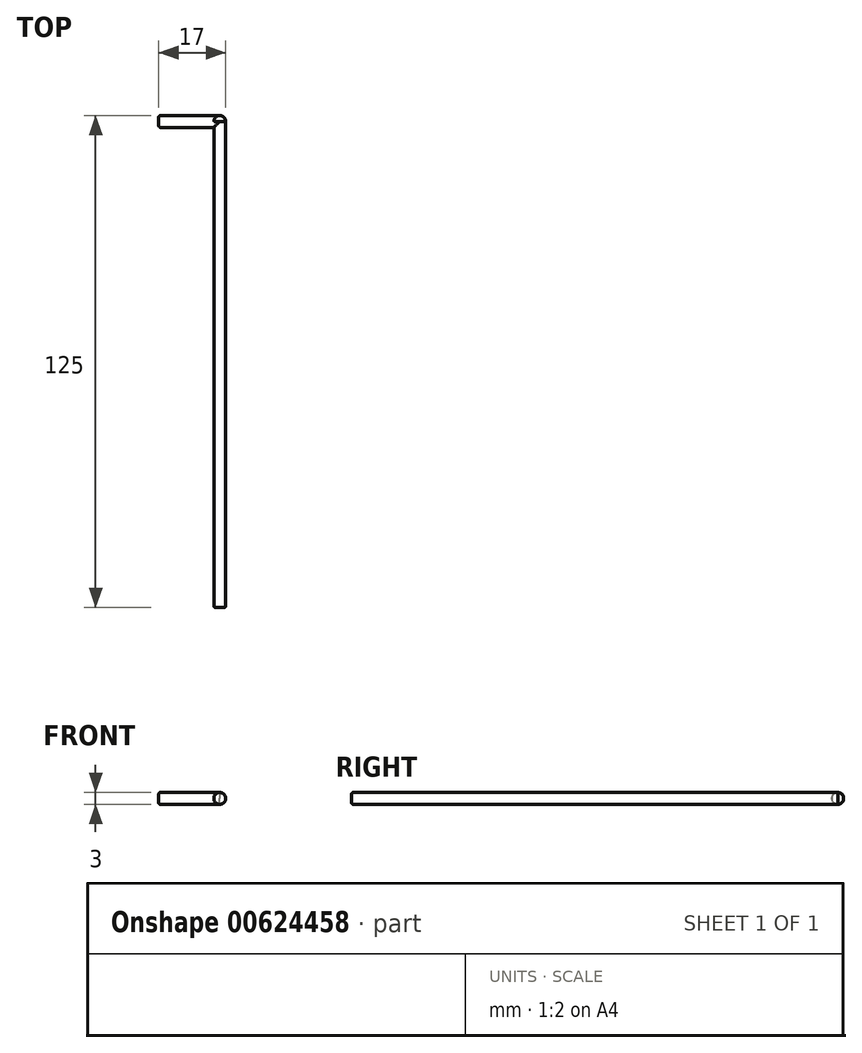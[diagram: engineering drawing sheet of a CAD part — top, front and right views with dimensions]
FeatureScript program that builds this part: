
annotation { "Feature Type Name" : "Feature", "Feature Type Description" : "" }
export const myFeature = defineFeature(function(context is Context, id is Id, definition is map)
    precondition{}
    {
        {
            var Q0;
            Q0=qCreatedBy(makeId("Front.planeOp"),FACE);
            var sketch = newSketch(context, id + "F0", { "sketchPlane" : qUnion([Q0])});
            skCircle(sketch, "E0", {"center": v(0, 0) * mm, "radius": 1.5 * mm});
            skSolve(sketch);
        }
        {
            var Q0;
            Q0=makeQuery(id+"F0.imprint","IMPRINT",FACE,{"disambiguationData":[TD([[makeQuery(id+"F0.imprint","IMPRINT",EDGE,{"derivedFrom":sQuery(id+"F0.wireOp",EDGE,"E0")}),1.0]])]});
            extrude(context, id + "F1", {"entities" : qUnion([Q0]), "depth" : 125 * mm, "offsetDistance" : 25.4 * mm});
        }
        {
            var Q0;
            Q0=qCreatedBy(makeId("Right.planeOp"),FACE);
            var sketch = newSketch(context, id + "F2", { "sketchPlane" : qUnion([Q0])});
            skCircle(sketch, "E1", {"center": v(-1.5, 0) * mm, "radius": 1.5 * mm});
            skSolve(sketch);
        }
        {
            var Q0;
            Q0 = qSketchRegion(id + "F2", true);
            extrude(context, id + "F3", {"entities" : qUnion([Q0]), "operationType" : NewBodyOperationType.ADD, "oppositeDirection" : true, "depth" : 15.5 * mm, "offsetDistance" : 25 * mm});
        }
        {
            var Q0;
            Q0=makeQuery(id+"F1.opExtrude","CAP_EDGE",EDGE,{"disambiguationData":[OSD([sQuery(id+"F0.wireOp",EDGE,"E0")])],"isStart":true});
            fillet(context, id + "F4", {"entities" : qUnion([Q0]), "radius" : 1.5 * mm, "tangentPropagation" : true, "allowEdgeOverflow" : false});
        }
        {
            var Q0;
            Q0=makeQuery(id+"F1.opExtrude","CAP_EDGE",EDGE,{"disambiguationData":[OSD([sQuery(id+"F0.wireOp",EDGE,"E0")])],"isStart":false});
            var Q1;
            Q1=makeQuery(id+"F3.opExtrude","CAP_EDGE",EDGE,{"disambiguationData":[OSD([sQuery(id+"F2.wireOp",EDGE,"E1")])],"isStart":false});
            fillet(context, id + "F5", {"entities" : qUnion([Q0, Q1]), "radius" : .4 * mm, "tangentPropagation" : true, "allowEdgeOverflow" : false});
        }
    });
